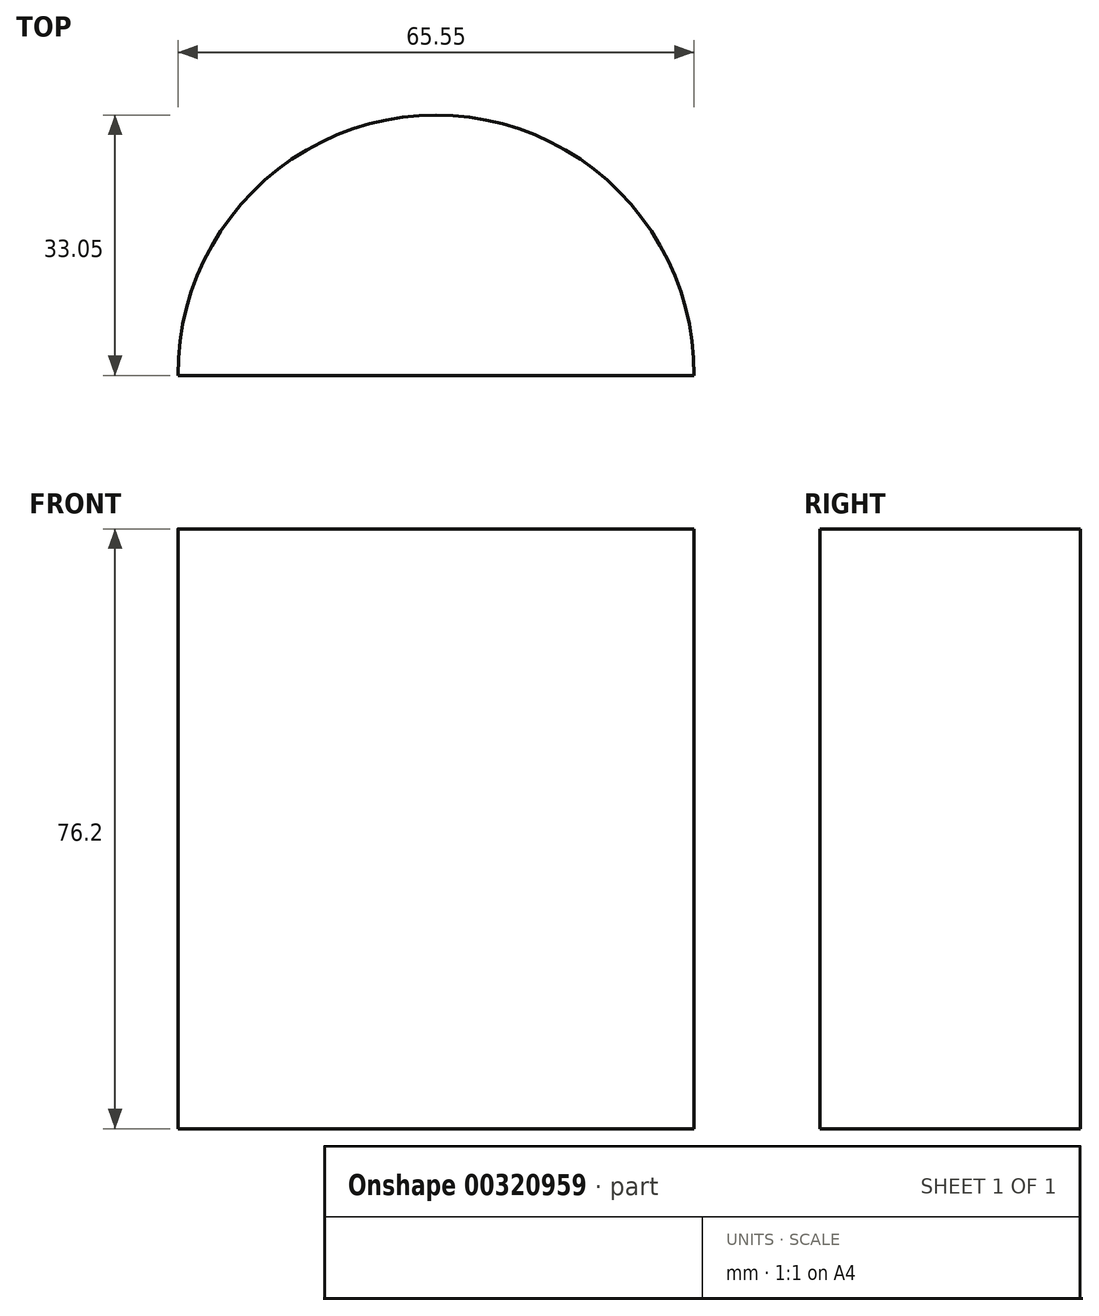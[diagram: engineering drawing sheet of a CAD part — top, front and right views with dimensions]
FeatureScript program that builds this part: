
annotation { "Feature Type Name" : "Feature", "Feature Type Description" : "" }
export const myFeature = defineFeature(function(context is Context, id is Id, definition is map)
    precondition{}
    {
        {
            var Q0;
            Q0=qCreatedBy(makeId("Top.planeOp"),FACE);
            var sketch = newSketch(context, id + "F0", { "sketchPlane" : qUnion([Q0])});
            skLineSegment(sketch, "E0", {"start": v(0, 0) * mm, "end": v(65.55, 0) * mm});
            skArc(sketch, "E1", {"start": v(65.55, 0) * mm, "mid": v(32.78, 33.05) * mm, "end": v(0, 0) * mm});
            skSolve(sketch);
        }
        {
            var Q0;
            Q0=makeQuery(id+"F0.imprint","IMPRINT",FACE,{"disambiguationData":[TD([[makeQuery(id+"F0.imprint","IMPRINT",EDGE,{"derivedFrom":sQuery(id+"F0.wireOp",EDGE,"E0")}),1.0]])]});
            extrude(context, id + "F1", {"entities" : qUnion([Q0]), "endBound" : BoundingType.SYMMETRIC, "depth" : 76.2 * mm});
        }
    });
